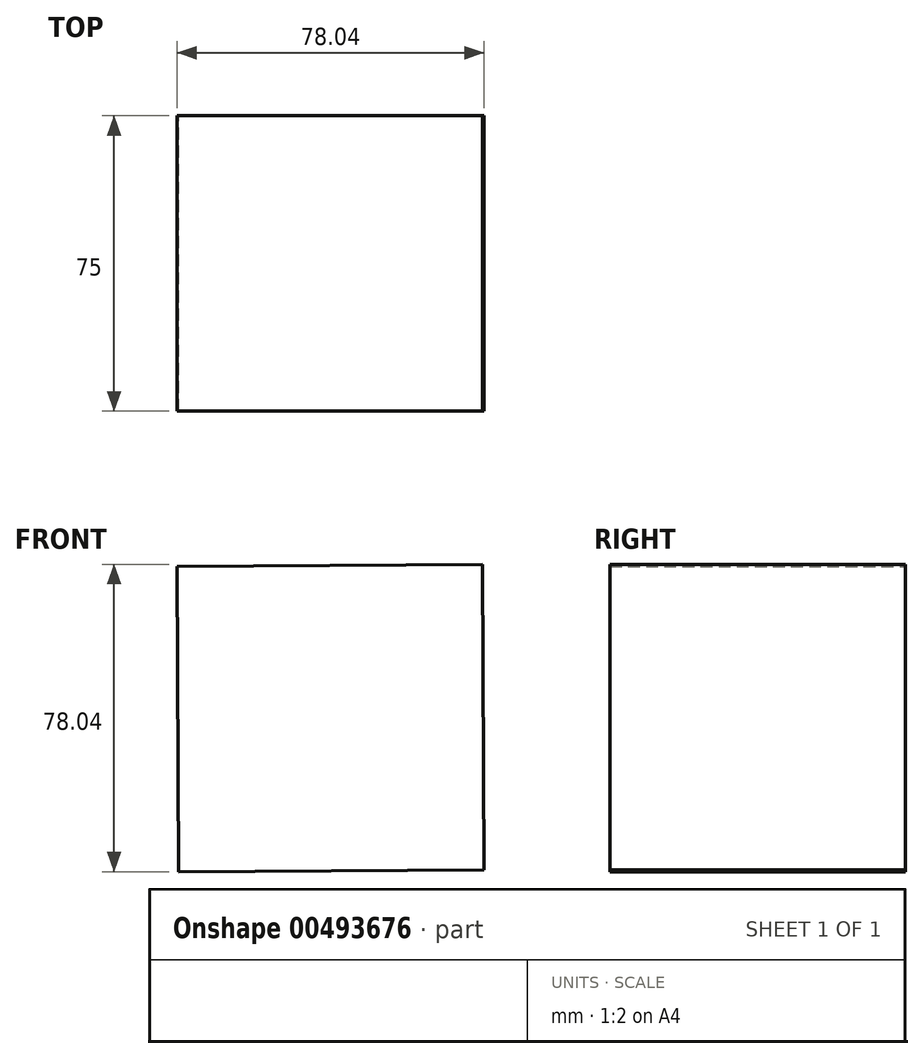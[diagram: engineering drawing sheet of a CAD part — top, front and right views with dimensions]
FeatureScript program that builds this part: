
annotation { "Feature Type Name" : "Feature", "Feature Type Description" : "" }
export const myFeature = defineFeature(function(context is Context, id is Id, definition is map)
    precondition{}
    {
        {
            var Q0;
            Q0=qCreatedBy(makeId("Front.planeOp"),FACE);
            var sketch = newSketch(context, id + "F0", { "sketchPlane" : qUnion([Q0])});
            skCircle(sketch, "E0.cCircle", {"center": v(0, 0) * mm, "radius": 54.87 * mm, "construction": true});
            skLineSegment(sketch, "E0.0", {"start": v(39.02, -38.59) * mm, "end": v(-38.59, -39.02) * mm});
            skLineSegment(sketch, "E0.1", {"start": v(-38.59, -39.02) * mm, "end": v(-39.02, 38.59) * mm});
            skLineSegment(sketch, "E0.2", {"start": v(-39.02, 38.59) * mm, "end": v(38.59, 39.02) * mm});
            skLineSegment(sketch, "E0.3", {"start": v(38.59, 39.02) * mm, "end": v(39.02, -38.59) * mm});
            skSolve(sketch);
        }
        {
            var Q0;
            Q0=makeQuery(id+"F0.imprint","IMPRINT",FACE,{"disambiguationData":[TD([[makeQuery(id+"F0.imprint","IMPRINT",EDGE,{"derivedFrom":sQuery(id+"F0.wireOp",EDGE,"E0.0")}),-1.0]])]});
            extrude(context, id + "F1", {"entities" : qUnion([Q0]), "depth" : 75 * mm});
        }
    });
